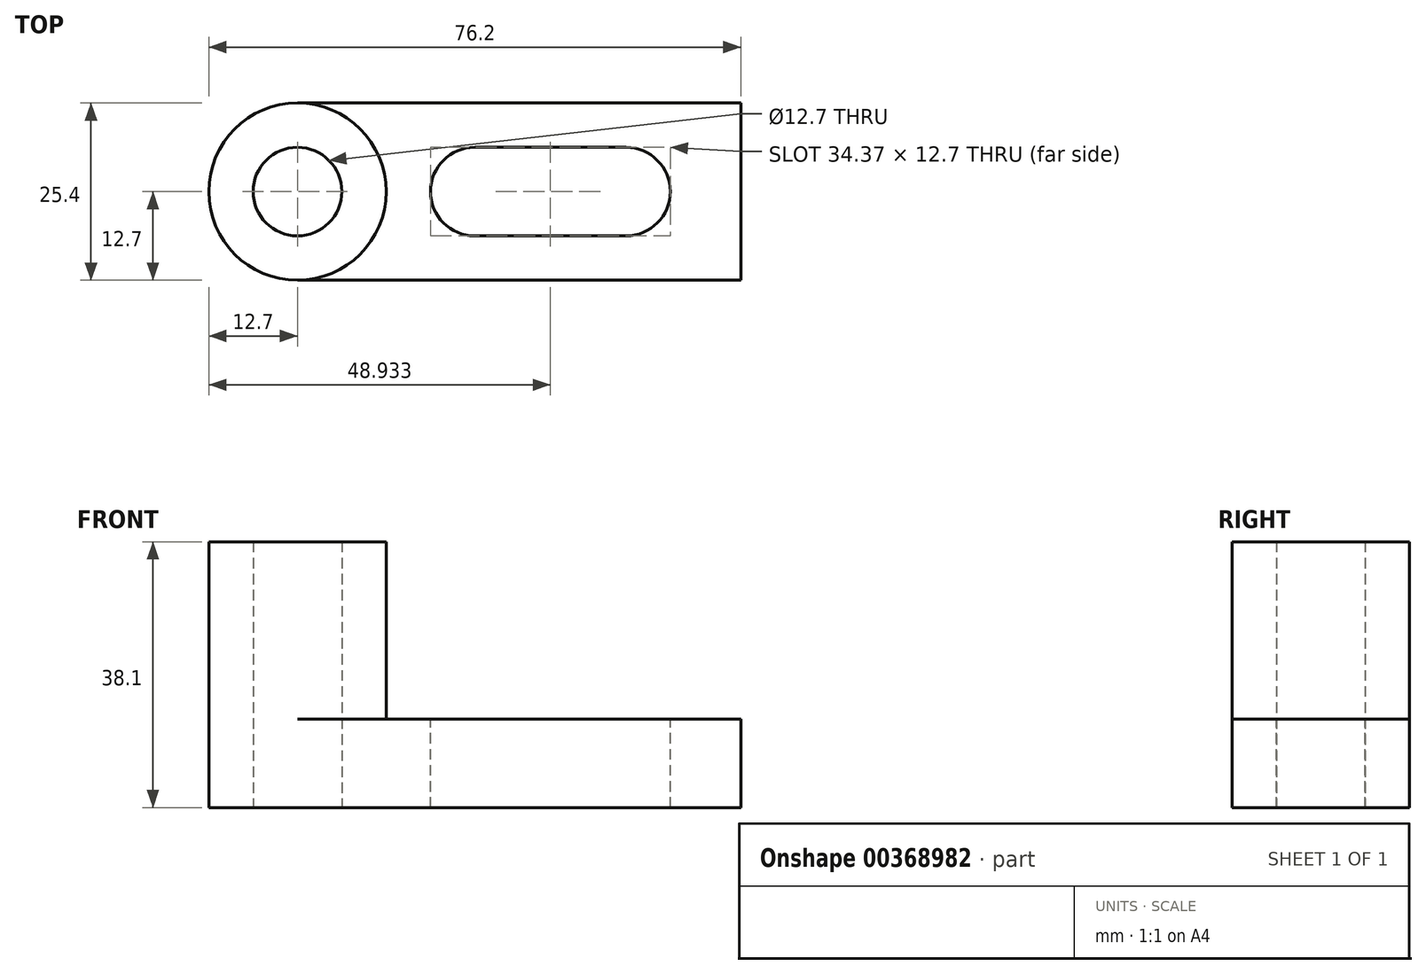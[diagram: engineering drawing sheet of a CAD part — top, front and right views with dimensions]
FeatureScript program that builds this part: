
annotation { "Feature Type Name" : "Feature", "Feature Type Description" : "" }
export const myFeature = defineFeature(function(context is Context, id is Id, definition is map)
    precondition{}
    {
        {
            var Q0;
            Q0=qCreatedBy(makeId("Top.planeOp"),FACE);
            var sketch = newSketch(context, id + "F0", { "sketchPlane" : qUnion([Q0])});
            skLineSegment(sketch, "E0", {"start": v(0, 25.4) * mm, "end": v(76.2, 25.4) * mm});
            skLineSegment(sketch, "E1", {"start": v(76.2, 25.4) * mm, "end": v(76.2, 0) * mm});
            skLineSegment(sketch, "E2", {"start": v(76.2, 0) * mm, "end": v(0, 0) * mm});
            skLineSegment(sketch, "E3", {"start": v(0, 0) * mm, "end": v(0, 25.4) * mm});
            skCircle(sketch, "E4", {"center": v(12.7, 12.7) * mm, "radius": 12.7 * mm});
            skPoint(sketch, "E4.centerSnap0", {"position": v(0, 12.7) * mm});
            skCircle(sketch, "E5", {"center": v(12.7, 12.7) * mm, "radius": 6.35 * mm});
            skSolve(sketch);
        }
        {
            var Q0;
            Q0=makeQuery(id+"F0.imprint","IMPRINT",FACE,{"disambiguationData":[TD([[makeQuery(id+"F0.imprint","IMPRINT",EDGE,{"derivedFrom":sQuery(id+"F0.wireOp",EDGE,"E5")}),-1.0]])]});
            extrude(context, id + "F1", {"entities" : qUnion([Q0]), "depth" : 38.1 * mm});
        }
        {
            var Q0;
            Q0=qCreatedBy(makeId("Top.planeOp"),FACE);
            var sketch = newSketch(context, id + "F2", { "sketchPlane" : qUnion([Q0])});
            skLineSegment(sketch, "E6", {"start": v(0, 25.4) * mm, "end": v(76.2, 25.4) * mm});
            skLineSegment(sketch, "E7", {"start": v(76.2, 25.4) * mm, "end": v(76.2, 0) * mm});
            skLineSegment(sketch, "E8", {"start": v(76.2, 0) * mm, "end": v(0, 0) * mm});
            skLineSegment(sketch, "E9", {"start": v(0, 0) * mm, "end": v(0, 25.4) * mm});
            skSolve(sketch);
        }
        {
            var Q0;
            Q0=makeQuery(id+"F2.imprint","IMPRINT",FACE,{"disambiguationData":[TD([[makeQuery(id+"F2.imprint","IMPRINT",EDGE,{"derivedFrom":sQuery(id+"F2.wireOp",EDGE,"E6")}),-1.0]])]});
            extrude(context, id + "F3", {"entities" : qUnion([Q0]), "operationType" : NewBodyOperationType.ADD, "depth" : 12.7 * mm});
        }
        {
            var Q0;
            {var subQ0=sQuery(id+"F2.wireOp",EDGE,"E9");var subQ1=sQuery(id+"F2.wireOp",EDGE,"E6");var subQ2=makeQuery(id+"F3.opExtrude","CAP_FACE",FACE,{"disambiguationData":[OSD([subQ1,sQuery(id+"F2.wireOp",EDGE,"E7"),sQuery(id+"F2.wireOp",EDGE,"E8"),subQ0])],"isStart":false});Q0=makeQuery(id+"F3.boolean.opBoolean","SPLIT",FACE,{"disambiguationData":[TD([makeQuery(id+"F1.opExtrude","SWEPT_FACE",FACE,{"disambiguationData":[OSD([sQuery(id+"F0.wireOp",EDGE,"E4")])]}),makeQuery(id+"F3.opExtrude","SWEPT_FACE",FACE,{"disambiguationData":[OSD([subQ1])]}),subQ2,makeQuery(id+"F3.opExtrude","SWEPT_FACE",FACE,{"disambiguationData":[OSD([subQ0])]})])],"derivedFrom":subQ2});}
            var Q1;
            {var subQ0=sQuery(id+"F2.wireOp",EDGE,"E9");var subQ1=sQuery(id+"F2.wireOp",EDGE,"E8");var subQ2=makeQuery(id+"F3.opExtrude","CAP_FACE",FACE,{"disambiguationData":[OSD([sQuery(id+"F2.wireOp",EDGE,"E6"),sQuery(id+"F2.wireOp",EDGE,"E7"),subQ1,subQ0])],"isStart":false});Q1=makeQuery(id+"F3.boolean.opBoolean","SPLIT",FACE,{"disambiguationData":[TD([makeQuery(id+"F1.opExtrude","SWEPT_FACE",FACE,{"disambiguationData":[OSD([sQuery(id+"F0.wireOp",EDGE,"E4")])]}),subQ2,makeQuery(id+"F3.opExtrude","SWEPT_FACE",FACE,{"disambiguationData":[OSD([subQ1])]}),makeQuery(id+"F3.opExtrude","SWEPT_FACE",FACE,{"disambiguationData":[OSD([subQ0])]})])],"derivedFrom":subQ2});}
            var Q2;
            Q2=makeQuery(id+"F3.boolean.opBoolean","SPLIT",FACE,{"disambiguationData":[TD([makeQuery(id+"F1.opExtrude","SWEPT_FACE",FACE,{"disambiguationData":[OSD([sQuery(id+"F0.wireOp",EDGE,"E5")])]})])],"derivedFrom":makeQuery(id+"F3.opExtrude","CAP_FACE",FACE,{"disambiguationData":[OSD([sQuery(id+"F2.wireOp",EDGE,"E6"),sQuery(id+"F2.wireOp",EDGE,"E7"),sQuery(id+"F2.wireOp",EDGE,"E8"),sQuery(id+"F2.wireOp",EDGE,"E9")])],"isStart":false})});
            extrude(context, id + "F4", {"entities" : qUnion([Q0, Q1, Q2]), "operationType" : NewBodyOperationType.REMOVE, "oppositeDirection" : true, "depth" : 76.2 * mm});
        }
        {
            var Q0;
            {var subQ0=sQuery(id+"F2.wireOp",EDGE,"E7");var subQ1=sQuery(id+"F2.wireOp",EDGE,"E6");var subQ2=sQuery(id+"F2.wireOp",EDGE,"E8");var subQ3=makeQuery(id+"F3.opExtrude","CAP_FACE",FACE,{"disambiguationData":[OSD([subQ1,subQ0,subQ2,sQuery(id+"F2.wireOp",EDGE,"E9")])],"isStart":false});Q0=makeQuery(id+"F3.boolean.opBoolean","SPLIT",FACE,{"disambiguationData":[TD([makeQuery(id+"F1.opExtrude","SWEPT_FACE",FACE,{"disambiguationData":[OSD([sQuery(id+"F0.wireOp",EDGE,"E4")])]}),makeQuery(id+"F3.opExtrude","SWEPT_FACE",FACE,{"disambiguationData":[OSD([subQ1])]}),subQ3,makeQuery(id+"F3.opExtrude","SWEPT_FACE",FACE,{"disambiguationData":[OSD([subQ0])]}),makeQuery(id+"F3.opExtrude","SWEPT_FACE",FACE,{"disambiguationData":[OSD([subQ2])]})])],"derivedFrom":subQ3});}
            var sketch = newSketch(context, id + "F5", { "sketchPlane" : qUnion([Q0])});
            skCircle(sketch, "E10", {"center": v(38.1, 12.7) * mm, "radius": 6.35 * mm});
            skCircle(sketch, "E11", {"center": v(59.77, 12.7) * mm, "radius": 6.35 * mm});
            skLineSegment(sketch, "E12", {"start": v(59.77, 6.35) * mm, "end": v(38.1, 6.35) * mm});
            skLineSegment(sketch, "E13", {"start": v(38.1, 19.05) * mm, "end": v(59.77, 19.05) * mm});
            skArc(sketch, "E14", {"start": v(59.77, 0) * mm, "mid": v(76.49, 12.7) * mm, "end": v(59.77, 25.4) * mm});
            skSolve(sketch);
        }
        {
            var Q0;
            {var subQ0=sQuery(id+"F5.wireOp",EDGE,"E12");Q0=makeQuery(id+"F5.imprint","IMPRINT",FACE,{"disambiguationData":[TD([[makeQuery(id+"F5.imprint","IMPRINT",EDGE,{"derivedFrom":subQ0}),-1.0]])]});}
            var Q1;
            {var subQ0=sQuery(id+"F5.wireOp",EDGE,"E10");var subQ1=makeQuery(id+"F5.imprint","INTERSECT",VERTEX,{"derivedFrom":[subQ0,sQuery(id+"F5.wireOp",EDGE,"E12")]});Q1=makeQuery(id+"F5.imprint","IMPRINT",FACE,{"disambiguationData":[TD([[makeQuery(id+"F5.imprint","IMPRINT",EDGE,{"disambiguationData":[TD([[subQ1,1.0]])],"derivedFrom":subQ0}),1.0]])]});}
            var Q2;
            {var subQ0=sQuery(id+"F5.wireOp",EDGE,"E11");var subQ1=makeQuery(id+"F5.imprint","INTERSECT",VERTEX,{"derivedFrom":[subQ0,sQuery(id+"F5.wireOp",EDGE,"E12")]});Q2=makeQuery(id+"F5.imprint","IMPRINT",FACE,{"disambiguationData":[TD([[makeQuery(id+"F5.imprint","IMPRINT",EDGE,{"disambiguationData":[TD([[subQ1,1.0]])],"derivedFrom":subQ0}),1.0]])]});}
            var Q3;
            {var subQ0=sQuery(id+"F5.wireOp",EDGE,"E14");var subQ1=sQuery(id+"F2.wireOp",EDGE,"E7");var subQ2=makeQuery(id+"F3.opExtrude","CAP_EDGE",EDGE,{"disambiguationData":[OSD([subQ1])],"isStart":false});var subQ3=makeQuery(id+"F5.imprint","INTERSECT",VERTEX,{"disambiguationData":[OD(1.0)],"derivedFrom":[subQ2,subQ0]});Q3=makeQuery(id+"F5.imprint","IMPRINT",FACE,{"disambiguationData":[TD([[makeQuery(id+"F5.imprint","IMPRINT",EDGE,{"disambiguationData":[TD([[subQ3,-1.0]])],"derivedFrom":subQ0}),-1.0]])]});}
            var Q4;
            {var subQ0=sQuery(id+"F5.wireOp",EDGE,"E14");var subQ2=sQuery(id+"F2.wireOp",EDGE,"E7");var subQ5=makeQuery(id+"F3.opExtrude","CAP_EDGE",EDGE,{"disambiguationData":[OSD([subQ2])],"isStart":false});var subQ6=makeQuery(id+"F5.imprint","INTERSECT",VERTEX,{"disambiguationData":[OD(0.0)],"derivedFrom":[subQ5,subQ0]});Q4=makeQuery(id+"F5.imprint","IMPRINT",FACE,{"disambiguationData":[TD([[makeQuery(id+"F5.imprint","IMPRINT",EDGE,{"disambiguationData":[TD([[subQ6,1.0]])],"derivedFrom":subQ0}),-1.0]])]});}
            extrude(context, id + "F6", {"entities" : qUnion([Q0, Q1, Q2, Q3, Q4]), "operationType" : NewBodyOperationType.REMOVE, "oppositeDirection" : true, "depth" : 12.7 * mm});
        }
    });
